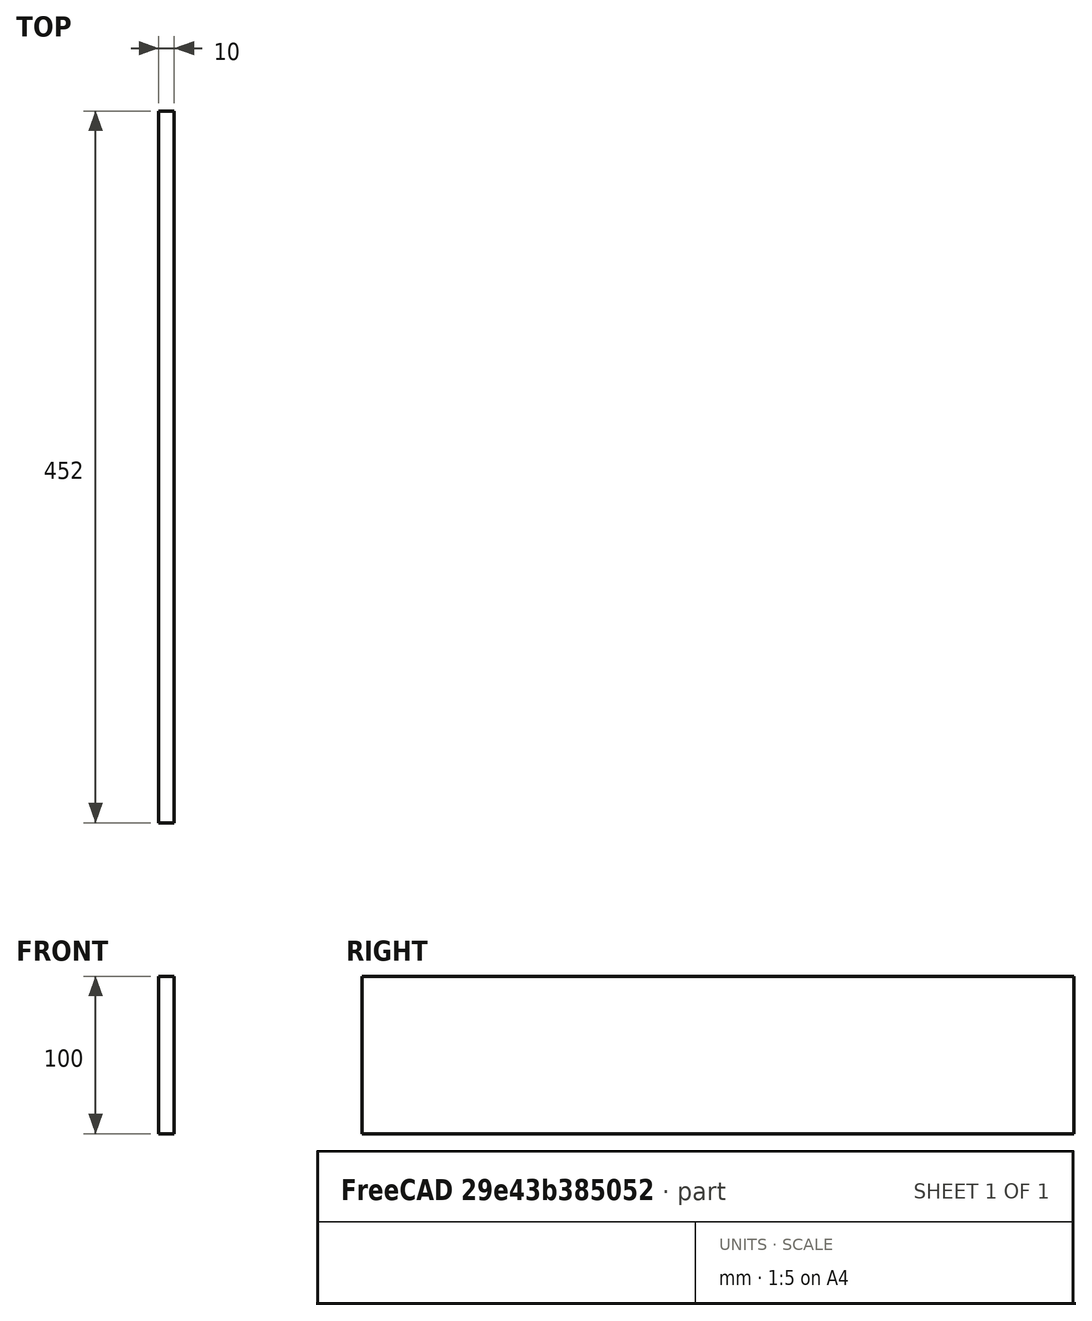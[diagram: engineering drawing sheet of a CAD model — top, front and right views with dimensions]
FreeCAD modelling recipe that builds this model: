
FCSTD DOCUMENT  (FreeCAD 0.19R24291 (Git))
Label: 500_Back_Horizontal_Mid
License: All rights reserved
LicenseURL: http://en.wikipedia.org/wiki/All_rights_reserved
objects: Sketcher::SketchObject×1, Spreadsheet::Sheet×1, PartDesign::Pad×1, PartDesign::Body×1
note: 4 computed .brp shape members not serialized (recipe doc carries the construction recipe); baked Part::Feature solids carry a one-line shape summary decoded from their .brp

FEATURE [Sketcher::SketchObject] Sketch
  FullyConstrained = true
  MapMode = 4
  Placement = pos=(0,0,0) rot=(0.57735,0.57735,0.57735;2.0944rad)
  Support = -> [XY_Plane]
  expr: Constraints[5] = Spreadsheet.nZ
  expr: Constraints[6] = Spreadsheet.nY
  sketch-geometry (5):
    g0: LineSegment StartX=0 StartY=0 StartZ=0 EndX=0 EndY=100 EndZ=0
    g1: LineSegment StartX=452 StartY=0 StartZ=0 EndX=452 EndY=100 EndZ=0
    g2: LineSegment StartX=452 StartY=100 StartZ=0 EndX=0 EndY=100 EndZ=0
    g3: LineSegment StartX=226 StartY=0 StartZ=0 EndX=0 EndY=0 EndZ=0
    g4: LineSegment StartX=452 StartY=0 StartZ=0 EndX=226 EndY=0 EndZ=0
  constraints (14):
    c: Vertical(g0)
    c: Vertical(g1)
    c: Coincident(g2,g1)
    c: Coincident(g2,g0)
    c: Horizontal(g2)
    c: DistanceY(g1,g1) = 100
    c: DistanceX(g2,g2) = 452
    c: Coincident(g3,g0)
    c: Coincident(g4,g1)
    c: Horizontal(g4)
    c: Equal(g3,g4)
    c: Coincident(g4,g3)
    c: Horizontal(g3)
    c: Coincident(g0,g-1)
FEATURE [Spreadsheet::Sheet] Spreadsheet  label="xls"
  cells = B7=KEYBOARD FRONT; B8=Width; C8=nY; D8(nY)==500 - 19 - 19 - 10; B9=Height; C9=nZ; D9(nZ)=100; E9=F(T); B10=Thickness; C10=nT; D10(nT)=10
FEATURE [PartDesign::Pad] Pad
  AllowMultiFace = false
  Direction = (1,1,1)
  Length = 10
  Length2 = 100
  Profile = -> Sketch
  Reversed = true
  Type = 0
  expr: Length = Spreadsheet.nT
FEATURE [PartDesign::Body] Body
  Group = -> [Sketch,Pad]
  Origin = -> Origin
  Tip = -> Pad
